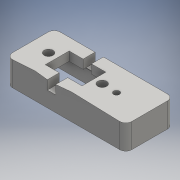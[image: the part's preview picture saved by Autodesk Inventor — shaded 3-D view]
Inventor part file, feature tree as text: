
AUTODESK INVENTOR PART (.ipt)
format: ipt  version: 2016 SP1 (Build 200210100, 210)  size: 194,048 bytes
history: native  units: mm
features: sketch x5, extrude x5, reference x2, plane x1
ambient origin geometry x8: Origin, YZ Plane, XZ Plane, XY Plane, X Axis, Y Axis, Z Axis, Center Point
bodies: Solid1 (feature_tree)
feature tree (13):
  plane  "Work Plane1"
  sketch  "Sketch1"  dims[d2=6.0mm d3=12.684184mm]
  extrude  "Extrusion4"  Depth=12.684184mm
  extrude  "Extrusion5"  Depth=7.0mm
  extrude  "Extrusion6"  Depth=6.0mm
  extrude  "Extrusion7"  Depth=3.0mm TaperAngle=0.0deg
  extrude  "Extrusion8"  Depth=4.0mm
  sketch  "Sketch5"  dims[d4=2.0mm d5=7.0mm]
  reference  "Reference11"
  reference  "Reference12"
  sketch  "Sketch6"  dims[d14=5.2mm d15=0.0mm d16=6.0mm]
  sketch  "Sketch7"  dims[d17=7.0mm d18=3.0mm d19=0.0mm]
  sketch  "Sketch8"  dims[d20=3.0mm d21=0.0mm d22=4.0mm d23=4.0mm d24=0.5mm d25=5.0mm d26=0.0mm d27=2.0mm d28=5.0mm d29=4.0mm d30=0.0mm d31=1.0mm]
